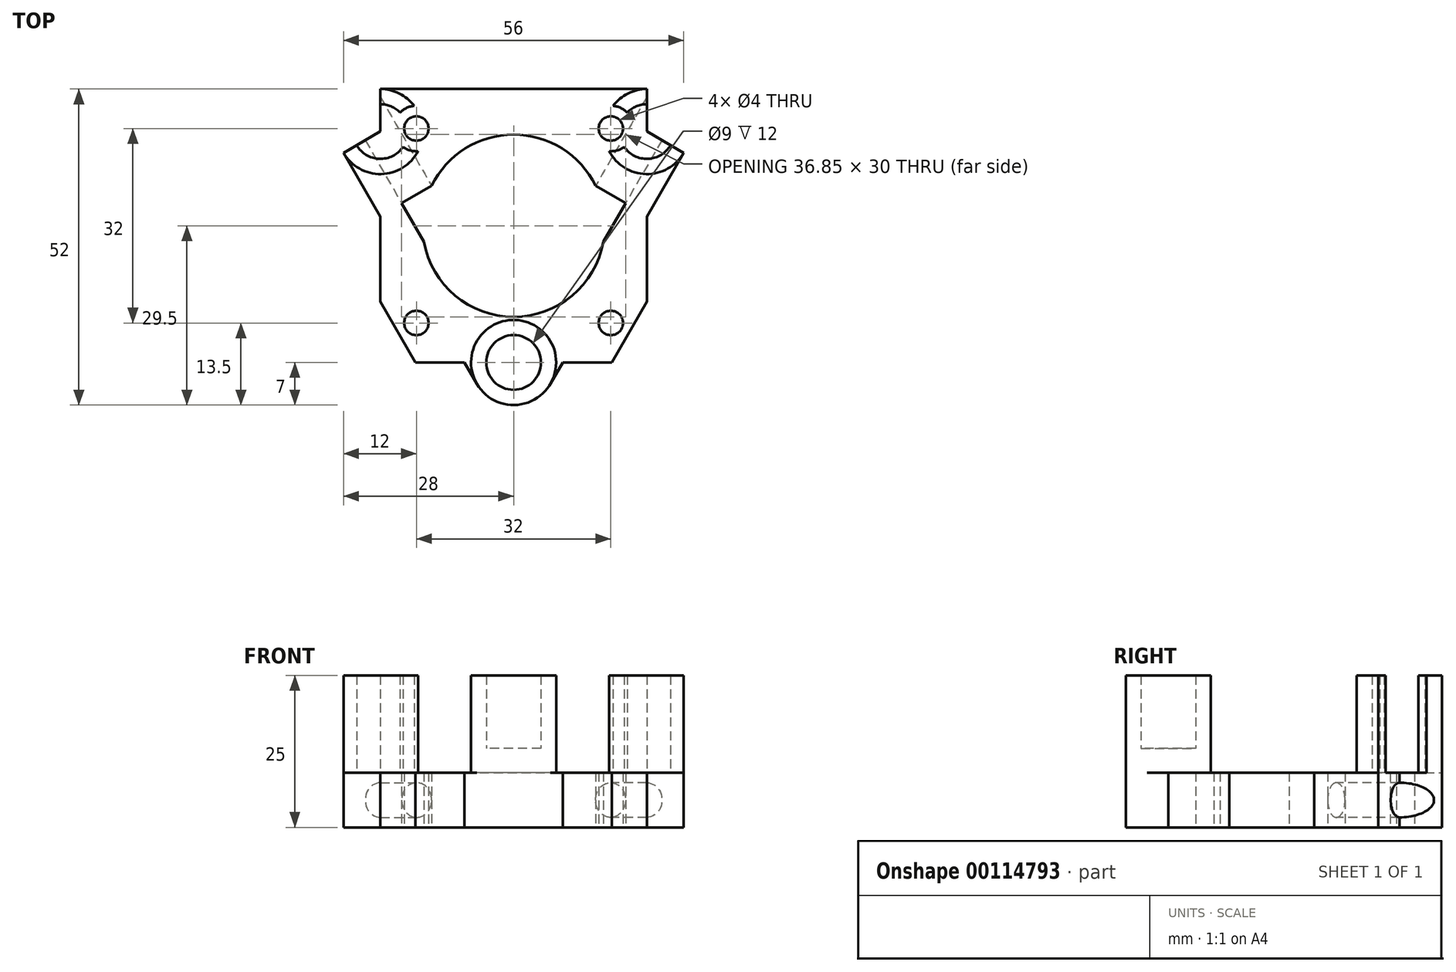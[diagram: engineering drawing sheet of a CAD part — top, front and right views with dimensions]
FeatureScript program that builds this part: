
annotation { "Feature Type Name" : "Feature", "Feature Type Description" : "" }
export const myFeature = defineFeature(function(context is Context, id is Id, definition is map)
    precondition{}
    {
        {
            var Q0;
            Q0=qCreatedBy(makeId("Top.planeOp"),FACE);
            var sketch = newSketch(context, id + "F0", { "sketchPlane" : qUnion([Q0])});
            skLineSegment(sketch, "E0", {"start": v(0, 0) * mm, "end": v(0, 38) * mm});
            skLineSegment(sketch, "E1", {"start": v(0, 0) * mm, "end": v(-21.94, 38) * mm});
            skCircle(sketch, "E2", {"center": v(-21.94, 38) * mm, "radius": 4.5 * mm});
            skCircle(sketch, "E3", {"center": v(-21.94, 38) * mm, "radius": 7 * mm});
            skCircle(sketch, "E4", {"center": v(0, 0) * mm, "radius": 7 * mm});
            skCircle(sketch, "E5", {"center": v(0, 0) * mm, "radius": 4.5 * mm});
            skLineSegment(sketch, "E6", {"start": v(0, 38) * mm, "end": v(0, 7) * mm});
            skPoint(sketch, "E7", {"position": v(0, 22.5) * mm});
            skCircle(sketch, "E8", {"center": v(-16, 38.5) * mm, "radius": 3.75 * mm});
            skCircle(sketch, "E9", {"center": v(-16, 6.5) * mm, "radius": 2 * mm});
            skCircle(sketch, "E10", {"center": v(-16, 38.5) * mm, "radius": 2 * mm});
            skLineSegment(sketch, "E11", {"start": v(0, 0) * mm, "end": v(-6.06, -3.5) * mm});
            skLineSegment(sketch, "E12", {"start": v(-21.94, 38) * mm, "end": v(-28, 34.5) * mm});
            skLineSegment(sketch, "E13", {"start": v(-6.06, -3.5) * mm, "end": v(-28, 34.5) * mm});
            skLineSegment(sketch, "E14.bottom", {"start": v(0, 0) * mm, "end": v(-21.94, 0) * mm});
            skLineSegment(sketch, "E14.top", {"start": v(0, 45) * mm, "end": v(-21.94, 45) * mm});
            skLineSegment(sketch, "E14.left", {"start": v(0, 0) * mm, "end": v(0, 45) * mm});
            skLineSegment(sketch, "E14.right", {"start": v(-21.94, 0) * mm, "end": v(-21.94, 45) * mm});
            skPoint(sketch, "E15", {"position": v(-16.17, 0) * mm});
            skPoint(sketch, "E16", {"position": v(-21.94, 10) * mm});
            skLineSegment(sketch, "E17", {"start": v(-21.94, 10) * mm, "end": v(-16.17, 0) * mm});
            skLineSegment(sketch, "E18", {"start": v(0, 31) * mm, "end": v(0, 7) * mm});
            skCircle(sketch, "E19", {"center": v(0, 22.5) * mm, "radius": 15 * mm});
            skLineSegment(sketch, "E20", {"start": v(0, 22.5) * mm, "end": v(-15.8, 13.37) * mm});
            skLineSegment(sketch, "E21", {"start": v(-15.96, 27.64) * mm, "end": v(-13.49, 29.06) * mm});
            skLineSegment(sketch, "E22", {"start": v(-15.96, 27.64) * mm, "end": v(-18.42, 26.21) * mm});
            skLineSegment(sketch, "E23", {"start": v(-18.42, 26.21) * mm, "end": v(-14.77, 19.88) * mm});
            skLineSegment(sketch, "E24", {"start": v(0, 0) * mm, "end": v(-0.61, -6.97) * mm});
            skLineSegment(sketch, "E25", {"start": v(0, 0) * mm, "end": v(0.61, -6.97) * mm});
            skSolve(sketch);
        }
        {
            var Q0;
            {var subQ0=sQuery(id+"F0.wireOp",EDGE,"E13");var subQ3=sQuery(id+"F0.wireOp",EDGE,"E14.right");var subQ5=makeQuery(id+"F0.imprint","INTERSECT",VERTEX,{"derivedFrom":[subQ0,subQ3]});Q0=makeQuery(id+"F0.imprint","IMPRINT",FACE,{"disambiguationData":[TD([[makeQuery(id+"F0.imprint","IMPRINT",EDGE,{"disambiguationData":[TD([[subQ5,-1.0]])],"derivedFrom":subQ3}),1.0]])]});}
            var Q1;
            {var subQ0=sQuery(id+"F0.wireOp",EDGE,"E5");var subQ1=sQuery(id+"F0.wireOp",EDGE,"E1");var subQ2=makeQuery(id+"F0.imprint","INTERSECT",VERTEX,{"derivedFrom":[subQ1,subQ0]});Q1=makeQuery(id+"F0.imprint","IMPRINT",FACE,{"disambiguationData":[TD([[makeQuery(id+"F0.imprint","IMPRINT",EDGE,{"disambiguationData":[TD([[subQ2,-1.0]])],"derivedFrom":subQ1}),-1.0]])]});}
            var Q2;
            {var subQ0=sQuery(id+"F0.wireOp",EDGE,"E3");var subQ1=sQuery(id+"F0.wireOp",EDGE,"E1");var subQ2=makeQuery(id+"F0.imprint","INTERSECT",VERTEX,{"derivedFrom":[subQ1,subQ0]});Q2=makeQuery(id+"F0.imprint","IMPRINT",FACE,{"disambiguationData":[TD([[makeQuery(id+"F0.imprint","IMPRINT",EDGE,{"disambiguationData":[TD([[subQ2,-1.0]])],"derivedFrom":subQ1}),-1.0]])]});}
            var Q3;
            {var subQ3=sQuery(id+"F0.wireOp",EDGE,"E4");var subQ7=sQuery(id+"F0.wireOp",EDGE,"E1");var subQ8=makeQuery(id+"F0.imprint","INTERSECT",VERTEX,{"derivedFrom":[subQ7,subQ3]});Q3=makeQuery(id+"F0.imprint","IMPRINT",FACE,{"disambiguationData":[TD([[makeQuery(id+"F0.imprint","IMPRINT",EDGE,{"disambiguationData":[TD([[subQ8,-1.0]])],"derivedFrom":subQ7}),1.0]])]});}
            var Q4;
            {var subQ0=sQuery(id+"F0.wireOp",EDGE,"E14.right");var subQ1=sQuery(id+"F0.wireOp",EDGE,"E2");var subQ2=makeQuery(id+"F0.imprint","INTERSECT",VERTEX,{"disambiguationData":[OD(0.0)],"derivedFrom":[subQ1,subQ0]});Q4=makeQuery(id+"F0.imprint","IMPRINT",FACE,{"disambiguationData":[TD([[makeQuery(id+"F0.imprint","IMPRINT",EDGE,{"disambiguationData":[TD([[subQ2,-1.0]])],"derivedFrom":subQ1}),1.0]])]});}
            var Q5;
            {var subQ0=sQuery(id+"F0.wireOp",EDGE,"E5");var subQ1=sQuery(id+"F0.wireOp",EDGE,"E1");var subQ2=makeQuery(id+"F0.imprint","INTERSECT",VERTEX,{"derivedFrom":[subQ1,subQ0]});Q5=makeQuery(id+"F0.imprint","IMPRINT",FACE,{"disambiguationData":[TD([[makeQuery(id+"F0.imprint","IMPRINT",EDGE,{"disambiguationData":[TD([[subQ2,-1.0]])],"derivedFrom":subQ1}),1.0]])]});}
            var Q6;
            {var subQ0=sQuery(id+"F0.wireOp",EDGE,"E8");var subQ1=sQuery(id+"F0.wireOp",EDGE,"E2");var subQ2=makeQuery(id+"F0.imprint","INTERSECT",VERTEX,{"disambiguationData":[OD(1.0)],"derivedFrom":[subQ1,subQ0]});Q6=makeQuery(id+"F0.imprint","IMPRINT",FACE,{"disambiguationData":[TD([[makeQuery(id+"F0.imprint","IMPRINT",EDGE,{"disambiguationData":[TD([[subQ2,-1.0]])],"derivedFrom":subQ1}),-1.0]])]});}
            var Q7;
            {var subQ0=sQuery(id+"F0.wireOp",EDGE,"E12");var subQ1=sQuery(id+"F0.wireOp",EDGE,"E2");var subQ2=makeQuery(id+"F0.imprint","INTERSECT",VERTEX,{"derivedFrom":[subQ1,subQ0]});Q7=makeQuery(id+"F0.imprint","IMPRINT",FACE,{"disambiguationData":[TD([[makeQuery(id+"F0.imprint","IMPRINT",EDGE,{"disambiguationData":[TD([[subQ2,-1.0]])],"derivedFrom":subQ1}),1.0]])]});}
            var Q8;
            {var subQ3=sQuery(id+"F0.wireOp",EDGE,"E14.left");var subQ5=sQuery(id+"F0.wireOp",EDGE,"E5");var subQ6=makeQuery(id+"F0.imprint","INTERSECT",VERTEX,{"derivedFrom":[subQ5,subQ3]});Q8=makeQuery(id+"F0.imprint","IMPRINT",FACE,{"disambiguationData":[TD([[makeQuery(id+"F0.imprint","IMPRINT",EDGE,{"disambiguationData":[TD([[subQ6,1.0]])],"derivedFrom":subQ5}),-1.0]])]});}
            var Q9;
            {var subQ3=sQuery(id+"F0.wireOp",EDGE,"E14.bottom");var subQ5=sQuery(id+"F0.wireOp",EDGE,"E5");var subQ6=makeQuery(id+"F0.imprint","INTERSECT",VERTEX,{"derivedFrom":[subQ5,subQ3]});Q9=makeQuery(id+"F0.imprint","IMPRINT",FACE,{"disambiguationData":[TD([[makeQuery(id+"F0.imprint","IMPRINT",EDGE,{"disambiguationData":[TD([[subQ6,-1.0]])],"derivedFrom":subQ5}),-1.0]])]});}
            var Q10;
            {var subQ0=sQuery(id+"F0.wireOp",EDGE,"E14.left");var subQ1=sQuery(id+"F0.wireOp",EDGE,"E5");var subQ2=makeQuery(id+"F0.imprint","INTERSECT",VERTEX,{"derivedFrom":[subQ1,subQ0]});Q10=makeQuery(id+"F0.imprint","IMPRINT",FACE,{"disambiguationData":[TD([[makeQuery(id+"F0.imprint","IMPRINT",EDGE,{"disambiguationData":[TD([[subQ2,1.0]])],"derivedFrom":subQ1}),1.0]])]});}
            var Q11;
            {var subQ0=sQuery(id+"F0.wireOp",EDGE,"E14.bottom");var subQ1=sQuery(id+"F0.wireOp",EDGE,"E5");var subQ2=makeQuery(id+"F0.imprint","INTERSECT",VERTEX,{"derivedFrom":[subQ1,subQ0]});Q11=makeQuery(id+"F0.imprint","IMPRINT",FACE,{"disambiguationData":[TD([[makeQuery(id+"F0.imprint","IMPRINT",EDGE,{"disambiguationData":[TD([[subQ2,-1.0]])],"derivedFrom":subQ1}),1.0]])]});}
            var Q12;
            {var subQ0=sQuery(id+"F0.wireOp",EDGE,"E14.right");var subQ1=sQuery(id+"F0.wireOp",EDGE,"E2");var subQ2=makeQuery(id+"F0.imprint","INTERSECT",VERTEX,{"disambiguationData":[OD(0.0)],"derivedFrom":[subQ1,subQ0]});Q12=makeQuery(id+"F0.imprint","IMPRINT",FACE,{"disambiguationData":[TD([[makeQuery(id+"F0.imprint","IMPRINT",EDGE,{"disambiguationData":[TD([[subQ2,-1.0]])],"derivedFrom":subQ1}),-1.0]])]});}
            var Q13;
            {var subQ0=sQuery(id+"F0.wireOp",EDGE,"E8");var subQ1=sQuery(id+"F0.wireOp",EDGE,"E3");var subQ2=makeQuery(id+"F0.imprint","INTERSECT",VERTEX,{"disambiguationData":[OD(0.0)],"derivedFrom":[subQ1,subQ0]});Q13=makeQuery(id+"F0.imprint","IMPRINT",FACE,{"disambiguationData":[TD([[makeQuery(id+"F0.imprint","IMPRINT",EDGE,{"disambiguationData":[TD([[subQ2,1.0]])],"derivedFrom":subQ1}),-1.0]])]});}
            var Q14;
            {var subQ0=sQuery(id+"F0.wireOp",EDGE,"E8");var subQ1=sQuery(id+"F0.wireOp",EDGE,"E2");var subQ2=makeQuery(id+"F0.imprint","INTERSECT",VERTEX,{"disambiguationData":[OD(0.0)],"derivedFrom":[subQ1,subQ0]});Q14=makeQuery(id+"F0.imprint","IMPRINT",FACE,{"disambiguationData":[TD([[makeQuery(id+"F0.imprint","IMPRINT",EDGE,{"disambiguationData":[TD([[subQ2,1.0]])],"derivedFrom":subQ1}),1.0]])]});}
            var Q15;
            Q15=makeQuery(id+"F0.imprint","IMPRINT",FACE,{"disambiguationData":[TD([[makeQuery(id+"F0.imprint","IMPRINT",EDGE,{"derivedFrom":sQuery(id+"F0.wireOp",EDGE,"E9")}),-1.0]])]});
            var Q16;
            {var subQ1=sQuery(id+"F0.wireOp",EDGE,"E1");var subQ3=sQuery(id+"F0.wireOp",EDGE,"E2");var subQ4=makeQuery(id+"F0.imprint","INTERSECT",VERTEX,{"derivedFrom":[subQ1,subQ3]});Q16=makeQuery(id+"F0.imprint","IMPRINT",FACE,{"disambiguationData":[TD([[makeQuery(id+"F0.imprint","IMPRINT",EDGE,{"disambiguationData":[TD([[subQ4,1.0]])],"derivedFrom":subQ3}),1.0]])]});}
            var Q17;
            {var subQ0=sQuery(id+"F0.wireOp",EDGE,"E8");var subQ1=sQuery(id+"F0.wireOp",EDGE,"E2");var subQ2=makeQuery(id+"F0.imprint","INTERSECT",VERTEX,{"disambiguationData":[OD(0.0)],"derivedFrom":[subQ1,subQ0]});Q17=makeQuery(id+"F0.imprint","IMPRINT",FACE,{"disambiguationData":[TD([[makeQuery(id+"F0.imprint","IMPRINT",EDGE,{"disambiguationData":[TD([[subQ2,-1.0]])],"derivedFrom":subQ1}),-1.0]])]});}
            var Q18;
            {var subQ1=sQuery(id+"F0.wireOp",EDGE,"E1");var subQ3=sQuery(id+"F0.wireOp",EDGE,"E5");var subQ4=makeQuery(id+"F0.imprint","INTERSECT",VERTEX,{"derivedFrom":[subQ1,subQ3]});Q18=makeQuery(id+"F0.imprint","IMPRINT",FACE,{"disambiguationData":[TD([[makeQuery(id+"F0.imprint","IMPRINT",EDGE,{"disambiguationData":[TD([[subQ4,1.0]])],"derivedFrom":subQ3}),1.0]])]});}
            var Q19;
            {var subQ5=sQuery(id+"F0.wireOp",EDGE,"E14.top");Q19=makeQuery(id+"F0.imprint","IMPRINT",FACE,{"disambiguationData":[TD([[makeQuery(id+"F0.imprint","IMPRINT",EDGE,{"derivedFrom":subQ5}),1.0]])]});}
            var Q20;
            {var subQ0=sQuery(id+"F0.wireOp",EDGE,"E8");var subQ1=sQuery(id+"F0.wireOp",EDGE,"E2");var subQ2=makeQuery(id+"F0.imprint","INTERSECT",VERTEX,{"disambiguationData":[OD(0.0)],"derivedFrom":[subQ1,subQ0]});Q20=makeQuery(id+"F0.imprint","IMPRINT",FACE,{"disambiguationData":[TD([[makeQuery(id+"F0.imprint","IMPRINT",EDGE,{"disambiguationData":[TD([[subQ2,-1.0]])],"derivedFrom":subQ1}),1.0]])]});}
            var Q21;
            {var subQ0=sQuery(id+"F0.wireOp",EDGE,"E3");var subQ1=sQuery(id+"F0.wireOp",EDGE,"E1");var subQ2=makeQuery(id+"F0.imprint","INTERSECT",VERTEX,{"derivedFrom":[subQ1,subQ0]});Q21=makeQuery(id+"F0.imprint","IMPRINT",FACE,{"disambiguationData":[TD([[makeQuery(id+"F0.imprint","IMPRINT",EDGE,{"disambiguationData":[TD([[subQ2,-1.0]])],"derivedFrom":subQ1}),1.0]])]});}
            var Q22;
            {var subQ9=sQuery(id+"F0.wireOp",EDGE,"E22");Q22=makeQuery(id+"F0.imprint","IMPRINT",FACE,{"disambiguationData":[TD([[makeQuery(id+"F0.imprint","IMPRINT",EDGE,{"derivedFrom":subQ9}),-1.0]])]});}
            var Q23;
            {var subQ0=sQuery(id+"F0.wireOp",EDGE,"E4");var subQ1=sQuery(id+"F0.wireOp",EDGE,"E1");var subQ2=makeQuery(id+"F0.imprint","INTERSECT",VERTEX,{"derivedFrom":[subQ1,subQ0]});Q23=makeQuery(id+"F0.imprint","IMPRINT",FACE,{"disambiguationData":[TD([[makeQuery(id+"F0.imprint","IMPRINT",EDGE,{"disambiguationData":[TD([[subQ2,-1.0]])],"derivedFrom":subQ1}),-1.0]])]});}
            var Q24;
            {var subQ0=sQuery(id+"F0.wireOp",EDGE,"E8");var subQ1=sQuery(id+"F0.wireOp",EDGE,"E2");var subQ2=makeQuery(id+"F0.imprint","INTERSECT",VERTEX,{"disambiguationData":[OD(0.0)],"derivedFrom":[subQ1,subQ0]});Q24=makeQuery(id+"F0.imprint","IMPRINT",FACE,{"disambiguationData":[TD([[makeQuery(id+"F0.imprint","IMPRINT",EDGE,{"disambiguationData":[TD([[subQ2,1.0]])],"derivedFrom":subQ1}),-1.0]])]});}
            var Q25;
            {var subQ1=sQuery(id+"F0.wireOp",EDGE,"E1");var subQ3=sQuery(id+"F0.wireOp",EDGE,"E5");var subQ4=makeQuery(id+"F0.imprint","INTERSECT",VERTEX,{"derivedFrom":[subQ1,subQ3]});Q25=makeQuery(id+"F0.imprint","IMPRINT",FACE,{"disambiguationData":[TD([[makeQuery(id+"F0.imprint","IMPRINT",EDGE,{"disambiguationData":[TD([[subQ4,-1.0]])],"derivedFrom":subQ3}),1.0]])]});}
            var Q26;
            {var subQ0=sQuery(id+"F0.wireOp",EDGE,"E12");var subQ1=sQuery(id+"F0.wireOp",EDGE,"E2");var subQ2=makeQuery(id+"F0.imprint","INTERSECT",VERTEX,{"derivedFrom":[subQ1,subQ0]});Q26=makeQuery(id+"F0.imprint","IMPRINT",FACE,{"disambiguationData":[TD([[makeQuery(id+"F0.imprint","IMPRINT",EDGE,{"disambiguationData":[TD([[subQ2,-1.0]])],"derivedFrom":subQ1}),-1.0]])]});}
            var Q27;
            {var subQ0=sQuery(id+"F0.wireOp",EDGE,"E13");var subQ3=sQuery(id+"F0.wireOp",EDGE,"E14.bottom");var subQ5=makeQuery(id+"F0.imprint","INTERSECT",VERTEX,{"derivedFrom":[subQ0,subQ3]});Q27=makeQuery(id+"F0.imprint","IMPRINT",FACE,{"disambiguationData":[TD([[makeQuery(id+"F0.imprint","IMPRINT",EDGE,{"disambiguationData":[TD([[subQ5,1.0]])],"derivedFrom":subQ3}),1.0]])]});}
            var Q28;
            {var subQ0=sQuery(id+"F0.wireOp",EDGE,"E11");var subQ1=sQuery(id+"F0.wireOp",EDGE,"E5");var subQ2=makeQuery(id+"F0.imprint","INTERSECT",VERTEX,{"derivedFrom":[subQ1,subQ0]});Q28=makeQuery(id+"F0.imprint","IMPRINT",FACE,{"disambiguationData":[TD([[makeQuery(id+"F0.imprint","IMPRINT",EDGE,{"disambiguationData":[TD([[subQ2,-1.0]])],"derivedFrom":subQ1}),1.0]])]});}
            var Q29;
            {var subQ0=sQuery(id+"F0.wireOp",EDGE,"E11");var subQ5=sQuery(id+"F0.wireOp",EDGE,"E5");var subQ7=makeQuery(id+"F0.imprint","INTERSECT",VERTEX,{"derivedFrom":[subQ5,subQ0]});Q29=makeQuery(id+"F0.imprint","IMPRINT",FACE,{"disambiguationData":[TD([[makeQuery(id+"F0.imprint","IMPRINT",EDGE,{"disambiguationData":[TD([[subQ7,-1.0]])],"derivedFrom":subQ5}),-1.0]])]});}
            var Q30;
            {var subQ0=sQuery(id+"F0.wireOp",EDGE,"E24");var subQ1=sQuery(id+"F0.wireOp",EDGE,"E4");var subQ2=makeQuery(id+"F0.imprint","INTERSECT",VERTEX,{"derivedFrom":[subQ1,subQ0]});Q30=makeQuery(id+"F0.imprint","IMPRINT",FACE,{"disambiguationData":[TD([[makeQuery(id+"F0.imprint","IMPRINT",EDGE,{"disambiguationData":[TD([[subQ2,-1.0]])],"derivedFrom":subQ1}),1.0]])]});}
            var Q31;
            {var subQ0=sQuery(id+"F0.wireOp",EDGE,"E24");var subQ1=sQuery(id+"F0.wireOp",EDGE,"E5");var subQ2=makeQuery(id+"F0.imprint","INTERSECT",VERTEX,{"derivedFrom":[subQ1,subQ0]});Q31=makeQuery(id+"F0.imprint","IMPRINT",FACE,{"disambiguationData":[TD([[makeQuery(id+"F0.imprint","IMPRINT",EDGE,{"disambiguationData":[TD([[subQ2,-1.0]])],"derivedFrom":subQ1}),1.0]])]});}
            extrude(context, id + "F1", {"entities" : qUnion([Q0, Q1, Q2, Q3, Q4, Q5, Q6, Q7, Q8, Q9, Q10, Q11, Q12, Q13, Q14, Q15, Q16, Q17, Q18, Q19, Q20, Q21, Q22, Q23, Q24, Q25, Q26, Q27, Q28, Q29, Q30, Q31]), "depth" : 9 * mm});
        }
        {
            var Q0;
            {var subQ3=sQuery(id+"F0.wireOp",EDGE,"E14.left");var subQ5=sQuery(id+"F0.wireOp",EDGE,"E5");var subQ6=makeQuery(id+"F0.imprint","INTERSECT",VERTEX,{"derivedFrom":[subQ5,subQ3]});Q0=makeQuery(id+"F0.imprint","IMPRINT",FACE,{"disambiguationData":[TD([[makeQuery(id+"F0.imprint","IMPRINT",EDGE,{"disambiguationData":[TD([[subQ6,1.0]])],"derivedFrom":subQ5}),-1.0]])]});}
            var Q1;
            {var subQ0=sQuery(id+"F0.wireOp",EDGE,"E5");var subQ1=sQuery(id+"F0.wireOp",EDGE,"E1");var subQ2=makeQuery(id+"F0.imprint","INTERSECT",VERTEX,{"derivedFrom":[subQ1,subQ0]});Q1=makeQuery(id+"F0.imprint","IMPRINT",FACE,{"disambiguationData":[TD([[makeQuery(id+"F0.imprint","IMPRINT",EDGE,{"disambiguationData":[TD([[subQ2,-1.0]])],"derivedFrom":subQ1}),1.0]])]});}
            var Q2;
            {var subQ0=sQuery(id+"F0.wireOp",EDGE,"E3");var subQ1=sQuery(id+"F0.wireOp",EDGE,"E1");var subQ2=makeQuery(id+"F0.imprint","INTERSECT",VERTEX,{"derivedFrom":[subQ1,subQ0]});Q2=makeQuery(id+"F0.imprint","IMPRINT",FACE,{"disambiguationData":[TD([[makeQuery(id+"F0.imprint","IMPRINT",EDGE,{"disambiguationData":[TD([[subQ2,-1.0]])],"derivedFrom":subQ1}),-1.0]])]});}
            var Q3;
            {var subQ0=sQuery(id+"F0.wireOp",EDGE,"E3");var subQ1=sQuery(id+"F0.wireOp",EDGE,"E1");var subQ2=makeQuery(id+"F0.imprint","INTERSECT",VERTEX,{"derivedFrom":[subQ1,subQ0]});Q3=makeQuery(id+"F0.imprint","IMPRINT",FACE,{"disambiguationData":[TD([[makeQuery(id+"F0.imprint","IMPRINT",EDGE,{"disambiguationData":[TD([[subQ2,-1.0]])],"derivedFrom":subQ1}),1.0]])]});}
            var Q4;
            {var subQ0=sQuery(id+"F0.wireOp",EDGE,"E12");var subQ1=sQuery(id+"F0.wireOp",EDGE,"E2");var subQ2=makeQuery(id+"F0.imprint","INTERSECT",VERTEX,{"derivedFrom":[subQ1,subQ0]});Q4=makeQuery(id+"F0.imprint","IMPRINT",FACE,{"disambiguationData":[TD([[makeQuery(id+"F0.imprint","IMPRINT",EDGE,{"disambiguationData":[TD([[subQ2,-1.0]])],"derivedFrom":subQ1}),-1.0]])]});}
            var Q5;
            {var subQ0=sQuery(id+"F0.wireOp",EDGE,"E14.right");var subQ1=sQuery(id+"F0.wireOp",EDGE,"E2");var subQ2=makeQuery(id+"F0.imprint","INTERSECT",VERTEX,{"disambiguationData":[OD(0.0)],"derivedFrom":[subQ1,subQ0]});Q5=makeQuery(id+"F0.imprint","IMPRINT",FACE,{"disambiguationData":[TD([[makeQuery(id+"F0.imprint","IMPRINT",EDGE,{"disambiguationData":[TD([[subQ2,-1.0]])],"derivedFrom":subQ1}),-1.0]])]});}
            var Q6;
            {var subQ0=sQuery(id+"F0.wireOp",EDGE,"E8");var subQ1=sQuery(id+"F0.wireOp",EDGE,"E2");var subQ2=makeQuery(id+"F0.imprint","INTERSECT",VERTEX,{"disambiguationData":[OD(0.0)],"derivedFrom":[subQ1,subQ0]});Q6=makeQuery(id+"F0.imprint","IMPRINT",FACE,{"disambiguationData":[TD([[makeQuery(id+"F0.imprint","IMPRINT",EDGE,{"disambiguationData":[TD([[subQ2,-1.0]])],"derivedFrom":subQ1}),-1.0]])]});}
            var Q7;
            {var subQ3=sQuery(id+"F0.wireOp",EDGE,"E14.bottom");var subQ5=sQuery(id+"F0.wireOp",EDGE,"E5");var subQ7=makeQuery(id+"F0.imprint","INTERSECT",VERTEX,{"derivedFrom":[subQ5,subQ3]});Q7=makeQuery(id+"F0.imprint","IMPRINT",FACE,{"disambiguationData":[TD([[makeQuery(id+"F0.imprint","IMPRINT",EDGE,{"disambiguationData":[TD([[subQ7,-1.0]])],"derivedFrom":subQ5}),-1.0]])]});}
            var Q8;
            {var subQ0=sQuery(id+"F0.wireOp",EDGE,"E5");var subQ1=sQuery(id+"F0.wireOp",EDGE,"E1");var subQ2=makeQuery(id+"F0.imprint","INTERSECT",VERTEX,{"derivedFrom":[subQ1,subQ0]});Q8=makeQuery(id+"F0.imprint","IMPRINT",FACE,{"disambiguationData":[TD([[makeQuery(id+"F0.imprint","IMPRINT",EDGE,{"disambiguationData":[TD([[subQ2,-1.0]])],"derivedFrom":subQ1}),-1.0]])]});}
            extrude(context, id + "F2", {"entities" : qUnion([Q0, Q1, Q2, Q3, Q4, Q5, Q6, Q7, Q8]), "operationType" : NewBodyOperationType.ADD, "depth" : 25 * mm});
        }
        {
            var Q0;
            Q0=makeQuery(id+"F1.opExtrude","SWEPT_FACE",FACE,{"disambiguationData":[OSD([sQuery(id+"F0.wireOp",EDGE,"E21"),sQuery(id+"F0.wireOp",EDGE,"E22")])]});
            var sketch = newSketch(context, id + "F3", { "sketchPlane" : qUnion([Q0])});
            skLineSegment(sketch, "E26", {"start": v(0, 9) * mm, "end": v(0, 0) * mm});
            skCircle(sketch, "E27", {"center": v(0, 4.5) * mm, "radius": 2.85 * mm});
            skSolve(sketch);
        }
        {
            var Q0;
            {var subQ0=sQuery(id+"F3.wireOp",EDGE,"E27");var subQ1=sQuery(id+"F3.wireOp",EDGE,"E26");var subQ2=makeQuery(id+"F3.imprint","INTERSECT",VERTEX,{"disambiguationData":[OD(0.0)],"derivedFrom":[subQ1,subQ0]});Q0=makeQuery(id+"F3.imprint","IMPRINT",FACE,{"disambiguationData":[TD([[makeQuery(id+"F3.imprint","IMPRINT",EDGE,{"disambiguationData":[TD([[subQ2,-1.0]])],"derivedFrom":subQ1}),1.0]])]});}
            var Q1;
            {var subQ0=sQuery(id+"F3.wireOp",EDGE,"E27");var subQ1=sQuery(id+"F3.wireOp",EDGE,"E26");var subQ2=makeQuery(id+"F3.imprint","INTERSECT",VERTEX,{"disambiguationData":[OD(0.0)],"derivedFrom":[subQ1,subQ0]});Q1=makeQuery(id+"F3.imprint","IMPRINT",FACE,{"disambiguationData":[TD([[makeQuery(id+"F3.imprint","IMPRINT",EDGE,{"disambiguationData":[TD([[subQ2,-1.0]])],"derivedFrom":subQ1}),-1.0]])]});}
            extrude(context, id + "F4", {"entities" : qUnion([Q0, Q1]), "operationType" : NewBodyOperationType.REMOVE, "oppositeDirection" : true, "depth" : 25 * mm});
        }
        {
            var Q0;
            Q0=makeQuery(id+"F1.opExtrude","SWEPT_BODY",BODY,{"disambiguationData":[OSD([sQuery(id+"F0.wireOp",EDGE,"E3"),sQuery(id+"F0.wireOp",EDGE,"E4"),sQuery(id+"F0.wireOp",EDGE,"E9"),sQuery(id+"F0.wireOp",EDGE,"E10"),sQuery(id+"F0.wireOp",EDGE,"E13"),sQuery(id+"F0.wireOp",EDGE,"E14.bottom"),sQuery(id+"F0.wireOp",EDGE,"E14.top"),sQuery(id+"F0.wireOp",EDGE,"E14.left"),sQuery(id+"F0.wireOp",EDGE,"E14.right"),sQuery(id+"F0.wireOp",EDGE,"E17"),sQuery(id+"F0.wireOp",EDGE,"E18"),sQuery(id+"F0.wireOp",EDGE,"E19"),sQuery(id+"F0.wireOp",EDGE,"E21"),sQuery(id+"F0.wireOp",EDGE,"E22"),sQuery(id+"F0.wireOp",EDGE,"E23")])]});
            var Q1;
            Q1=qCreatedBy(makeId("Right.planeOp"),FACE);
            mirror(context, id + "F5", {"operationType" : NewBodyOperationType.ADD, "entities" : qUnion([Q0]), "mirrorPlane" : qUnion([Q1])});
        }
        {
            var Q0;
            {var subQ0=sQuery(id+"F0.wireOp",EDGE,"E24");var subQ1=sQuery(id+"F0.wireOp",EDGE,"E5");var subQ2=makeQuery(id+"F0.imprint","INTERSECT",VERTEX,{"derivedFrom":[subQ1,subQ0]});Q0=makeQuery(id+"F0.imprint","IMPRINT",FACE,{"disambiguationData":[TD([[makeQuery(id+"F0.imprint","IMPRINT",EDGE,{"disambiguationData":[TD([[subQ2,-1.0]])],"derivedFrom":subQ1}),1.0]])]});}
            var Q1;
            {var subQ0=sQuery(id+"F0.wireOp",EDGE,"E24");var subQ1=sQuery(id+"F0.wireOp",EDGE,"E4");var subQ2=makeQuery(id+"F0.imprint","INTERSECT",VERTEX,{"derivedFrom":[subQ1,subQ0]});Q1=makeQuery(id+"F0.imprint","IMPRINT",FACE,{"disambiguationData":[TD([[makeQuery(id+"F0.imprint","IMPRINT",EDGE,{"disambiguationData":[TD([[subQ2,-1.0]])],"derivedFrom":subQ1}),1.0]])]});}
            var Q2;
            {var subQ0=sQuery(id+"F0.wireOp",EDGE,"E11");var subQ1=sQuery(id+"F0.wireOp",EDGE,"E5");var subQ2=makeQuery(id+"F0.imprint","INTERSECT",VERTEX,{"derivedFrom":[subQ1,subQ0]});Q2=makeQuery(id+"F0.imprint","IMPRINT",FACE,{"disambiguationData":[TD([[makeQuery(id+"F0.imprint","IMPRINT",EDGE,{"disambiguationData":[TD([[subQ2,-1.0]])],"derivedFrom":subQ1}),1.0]])]});}
            var Q3;
            {var subQ0=sQuery(id+"F0.wireOp",EDGE,"E14.left");var subQ1=sQuery(id+"F0.wireOp",EDGE,"E5");var subQ2=makeQuery(id+"F0.imprint","INTERSECT",VERTEX,{"derivedFrom":[subQ1,subQ0]});Q3=makeQuery(id+"F0.imprint","IMPRINT",FACE,{"disambiguationData":[TD([[makeQuery(id+"F0.imprint","IMPRINT",EDGE,{"disambiguationData":[TD([[subQ2,1.0]])],"derivedFrom":subQ1}),1.0]])]});}
            var Q4;
            {var subQ1=sQuery(id+"F0.wireOp",EDGE,"E1");var subQ3=sQuery(id+"F0.wireOp",EDGE,"E5");var subQ4=makeQuery(id+"F0.imprint","INTERSECT",VERTEX,{"derivedFrom":[subQ1,subQ3]});Q4=makeQuery(id+"F0.imprint","IMPRINT",FACE,{"disambiguationData":[TD([[makeQuery(id+"F0.imprint","IMPRINT",EDGE,{"disambiguationData":[TD([[subQ4,1.0]])],"derivedFrom":subQ3}),1.0]])]});}
            var Q5;
            {var subQ1=sQuery(id+"F0.wireOp",EDGE,"E1");var subQ3=sQuery(id+"F0.wireOp",EDGE,"E5");var subQ4=makeQuery(id+"F0.imprint","INTERSECT",VERTEX,{"derivedFrom":[subQ1,subQ3]});Q5=makeQuery(id+"F0.imprint","IMPRINT",FACE,{"disambiguationData":[TD([[makeQuery(id+"F0.imprint","IMPRINT",EDGE,{"disambiguationData":[TD([[subQ4,-1.0]])],"derivedFrom":subQ3}),1.0]])]});}
            var Q6;
            {var subQ0=sQuery(id+"F0.wireOp",EDGE,"E14.bottom");var subQ1=sQuery(id+"F0.wireOp",EDGE,"E5");var subQ2=makeQuery(id+"F0.imprint","INTERSECT",VERTEX,{"derivedFrom":[subQ1,subQ0]});Q6=makeQuery(id+"F0.imprint","IMPRINT",FACE,{"disambiguationData":[TD([[makeQuery(id+"F0.imprint","IMPRINT",EDGE,{"disambiguationData":[TD([[subQ2,-1.0]])],"derivedFrom":subQ1}),1.0]])]});}
            extrude(context, id + "F6", {"entities" : qUnion([Q0, Q1, Q2, Q3, Q4, Q5, Q6]), "operationType" : NewBodyOperationType.ADD, "depth" : 13 * mm});
        }
    });
